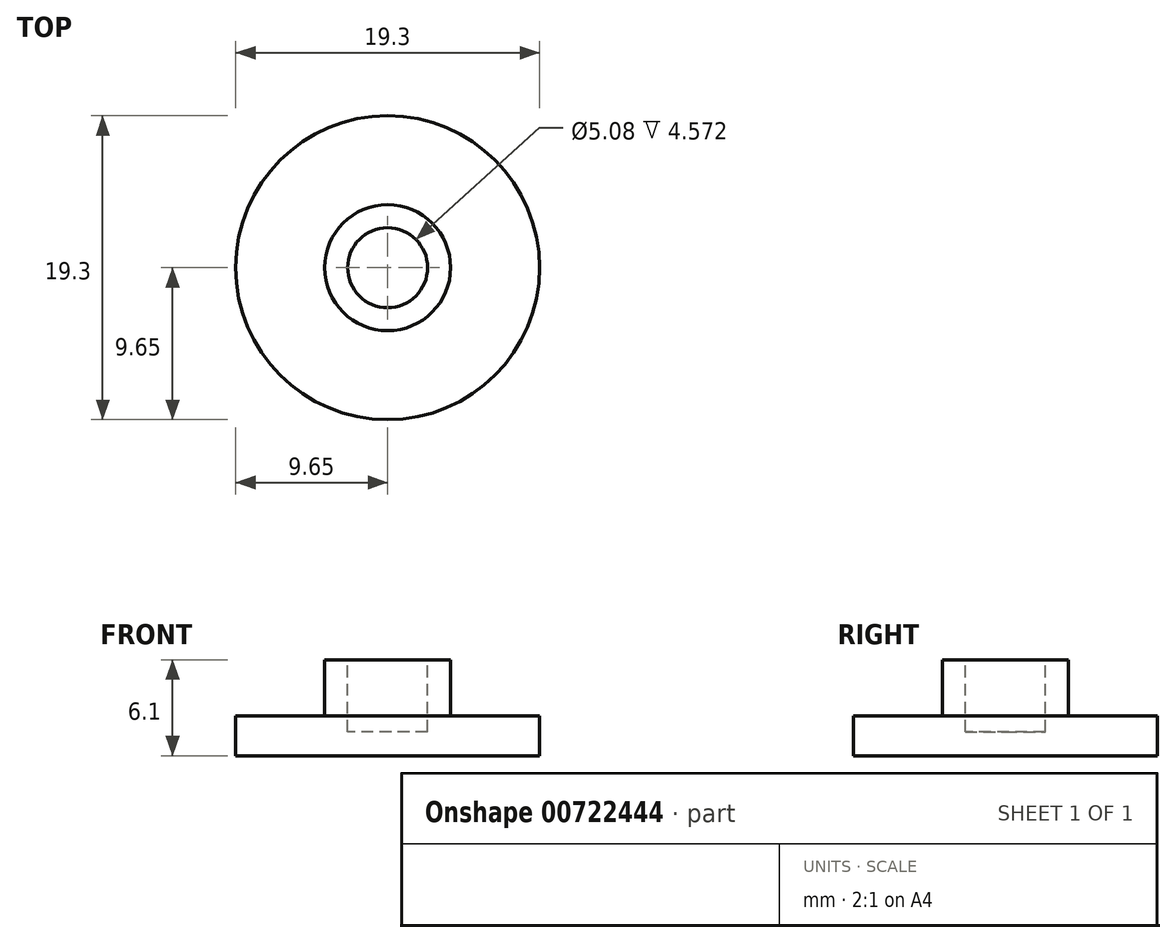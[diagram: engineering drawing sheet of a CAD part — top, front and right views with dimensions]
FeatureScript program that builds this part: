
annotation { "Feature Type Name" : "Feature", "Feature Type Description" : "" }
export const myFeature = defineFeature(function(context is Context, id is Id, definition is map)
    precondition{}
    {
        {
            var Q0;
            Q0=qCreatedBy(makeId("Top.planeOp"),FACE);
            var sketch = newSketch(context, id + "F0", { "sketchPlane" : qUnion([Q0])});
            skCircle(sketch, "E0", {"center": v(0, 0) * mm, "radius": 9.65 * mm});
            skCircle(sketch, "E1", {"center": v(0, 0) * mm, "radius": 3.87 * mm});
            skSolve(sketch);
        }
        {
            var Q0;
            Q0 = qSketchRegion(id + "F0", true);
            extrude(context, id + "F1", {"entities" : qUnion([Q0]), "depth" : 2.54 * mm, "offsetDistance" : 25.4 * mm});
        }
        {
            var Q0;
            Q0=qCreatedBy(makeId("Top.planeOp"),FACE);
            var sketch = newSketch(context, id + "F2", { "sketchPlane" : qUnion([Q0])});
            skCircle(sketch, "E2", {"center": v(0, 0) * mm, "radius": 4 * mm});
            skSolve(sketch);
        }
        {
            var Q0;
            Q0 = qSketchRegion(id + "F2", true);
            extrude(context, id + "F3", {"entities" : qUnion([Q0]), "operationType" : NewBodyOperationType.ADD, "depth" : 6.1 * mm, "offsetDistance" : 25.4 * mm});
        }
        {
            var Q0;
            Q0=makeQuery(id+"F3.opExtrude","CAP_FACE",FACE,{"disambiguationData":[OSD([sQuery(id+"F2.wireOp",EDGE,"E2")])],"isStart":false});
            var sketch = newSketch(context, id + "F4", { "sketchPlane" : qUnion([Q0])});
            skCircle(sketch, "E3", {"center": v(0, 0) * mm, "radius": 2.54 * mm});
            skSolve(sketch);
        }
        {
            var Q0;
            Q0 = qSketchRegion(id + "F4", true);
            extrude(context, id + "F5", {"entities" : qUnion([Q0]), "operationType" : NewBodyOperationType.REMOVE, "oppositeDirection" : true, "depth" : 4.57 * mm, "offsetDistance" : 25.4 * mm});
        }
    });
